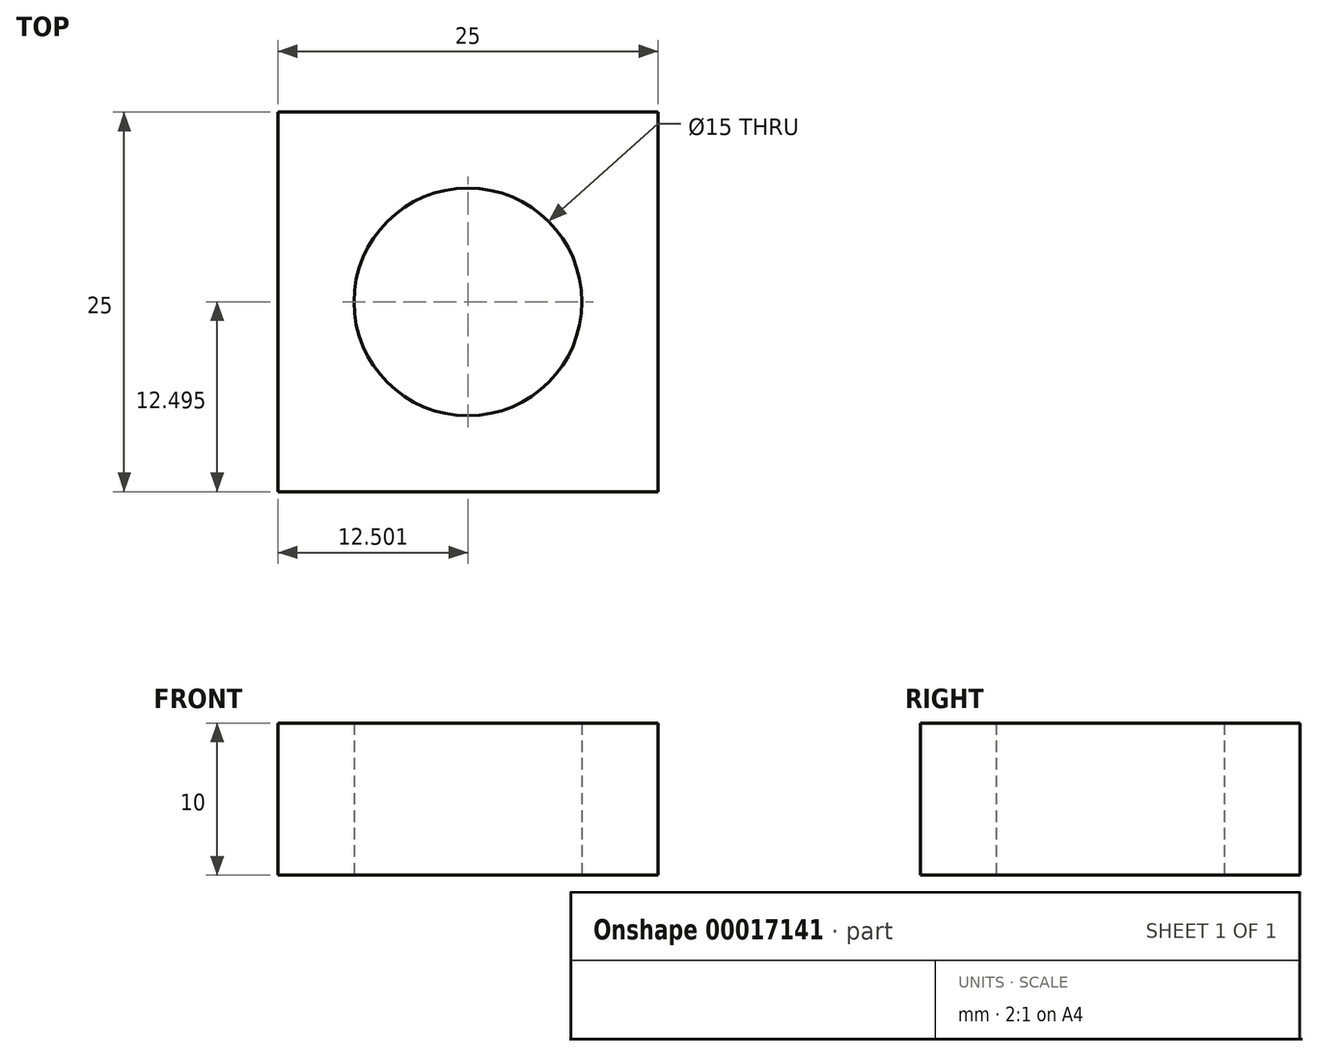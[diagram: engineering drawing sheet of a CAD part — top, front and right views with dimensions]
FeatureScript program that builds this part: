
annotation { "Feature Type Name" : "Feature", "Feature Type Description" : "" }
export const myFeature = defineFeature(function(context is Context, id is Id, definition is map)
    precondition{}
    {
        {
            var Q0;
            Q0=qCreatedBy(makeId("Top.planeOp"),FACE);
            var sketch = newSketch(context, id + "F0", { "sketchPlane" : qUnion([Q0])});
            skLineSegment(sketch, "E0.bottom", {"start": v(-3.2, -10.2) * mm, "end": v(-28.2, -10.2) * mm});
            skLineSegment(sketch, "E0.top", {"start": v(-3.2, -35.2) * mm, "end": v(-28.2, -35.2) * mm});
            skLineSegment(sketch, "E0.left", {"start": v(-3.2, -10.2) * mm, "end": v(-3.2, -35.2) * mm});
            skLineSegment(sketch, "E0.right", {"start": v(-28.2, -10.2) * mm, "end": v(-28.2, -35.2) * mm});
            skCircle(sketch, "E1", {"center": v(-15.7, -22.7) * mm, "radius": 7.5 * mm});
            skSolve(sketch);
        }
        {
            var Q0;
            Q0 = qSketchRegion(id + "F0", true);
            extrude(context, id + "F1", {"entities" : qUnion([Q0]), "depth" : 10 * mm});
        }
    });
